# Revit family: Shower-Valve_Trim-KOHLER-SINGULIER-K-10879T_1
name_source: partatom
category: Specialty Equipment
revit_build: Autodesk Revit 2017 (Build: 20160225_1515(x64)
units: mm (PartAtom-declared; Revit-internal decimal feet)

## family parameters
Cut with Voids When Loaded = No
Host = Face
OmniClass Number = 23.31.25.00
OmniClass Title = Toilet and Bath Specialties
Part Type = Normal
Room Calculation Point = No
Round Connector Dimension = Use Diameter
Shared = No

## types (3) — shared parameters
ADA Compliant = No
Assembly Code = C1030200
Date Modified = 03/31/2021
Default Elevation = 42"
Description = 40mm in-wall bathtub shower panel
Height = 6 11/16"
Length = 2 5/8"
Manufacturer = KOHLER Co.
Master Format 2014 = 10 28 00
Master Format 2014 Name = Toilet, Bath, and Laundry Accessories
Material = Primium metal construction
Product Documentation Link = https://files.kohler.com.cn
Product Name = SINGULIER
Product Page URL = https://www.kohler.com.cn
URL = https://www.kohler.com.cn
WaterSense Certified = No
Width = 4 9/16"

## per-type parameters (varying)
| type | Finish | Model | Type |
| AF-Flange Gold | Kohler-Metal-AF-Flange_Gold | K-10879T-4-AF | 2 |
| CP- Polished Chrome | Kohler-Metal-CP-Polished_Chrome | K-10879T-4-CP | 1 |
| BN-Roman Silver | Kohler-Metal-BN-Roman_Silver | K-10879T-4-BN | 3 |

## geometry (parser evidence)
native form markers: Sweep x4
no freeform markers — native parametric forms only
